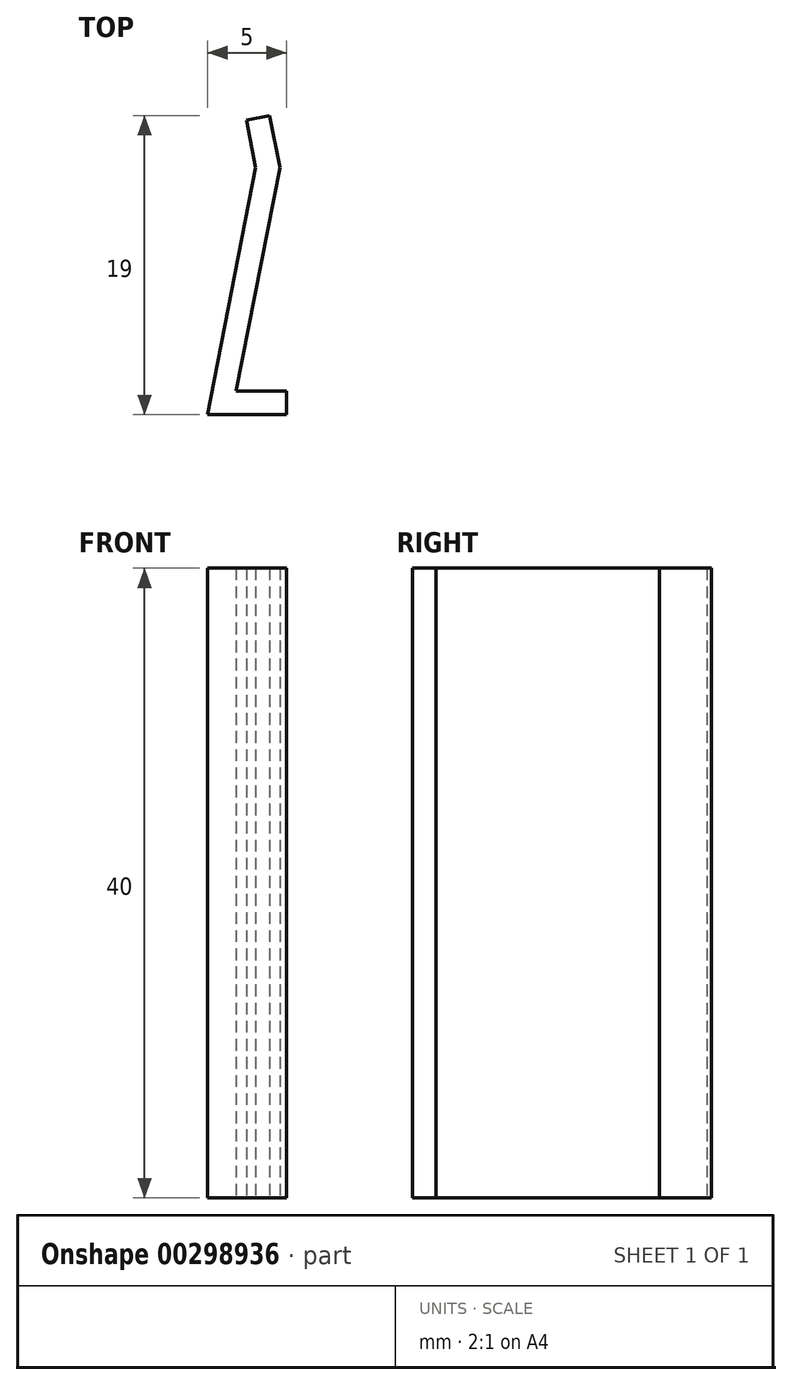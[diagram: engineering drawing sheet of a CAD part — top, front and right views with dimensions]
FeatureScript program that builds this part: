
annotation { "Feature Type Name" : "Feature", "Feature Type Description" : "" }
export const myFeature = defineFeature(function(context is Context, id is Id, definition is map)
    precondition{}
    {
        {
            var Q0;
            Q0=qCreatedBy(makeId("Top.planeOp"),FACE);
            var sketch = newSketch(context, id + "F0", { "sketchPlane" : qUnion([Q0])});
            skLineSegment(sketch, "E0", {"start": v(0, 0) * mm, "end": v(-5, 0) * mm});
            skLineSegment(sketch, "E1", {"start": v(-5, 0) * mm, "end": v(-1.95, 15.7) * mm});
            skLineSegment(sketch, "E2", {"start": v(-1.95, 15.7) * mm, "end": v(-2.53, 18.71) * mm});
            skLineSegment(sketch, "E3", {"start": v(-2.53, 18.71) * mm, "end": v(-1.06, 19) * mm});
            skLineSegment(sketch, "E4", {"start": v(-1.06, 19) * mm, "end": v(-0.42, 15.7) * mm});
            skLineSegment(sketch, "E5", {"start": v(-0.42, 15.7) * mm, "end": v(-3.18, 1.5) * mm});
            skLineSegment(sketch, "E6", {"start": v(-3.18, 1.5) * mm, "end": v(0, 1.5) * mm});
            skLineSegment(sketch, "E7", {"start": v(0, 1.5) * mm, "end": v(0, 0) * mm});
            skSolve(sketch);
        }
        {
            var Q0;
            Q0 = qSketchRegion(id + "F0", true);
            extrude(context, id + "F1", {"entities" : qUnion([Q0]), "depth" : 40 * mm});
        }
    });
